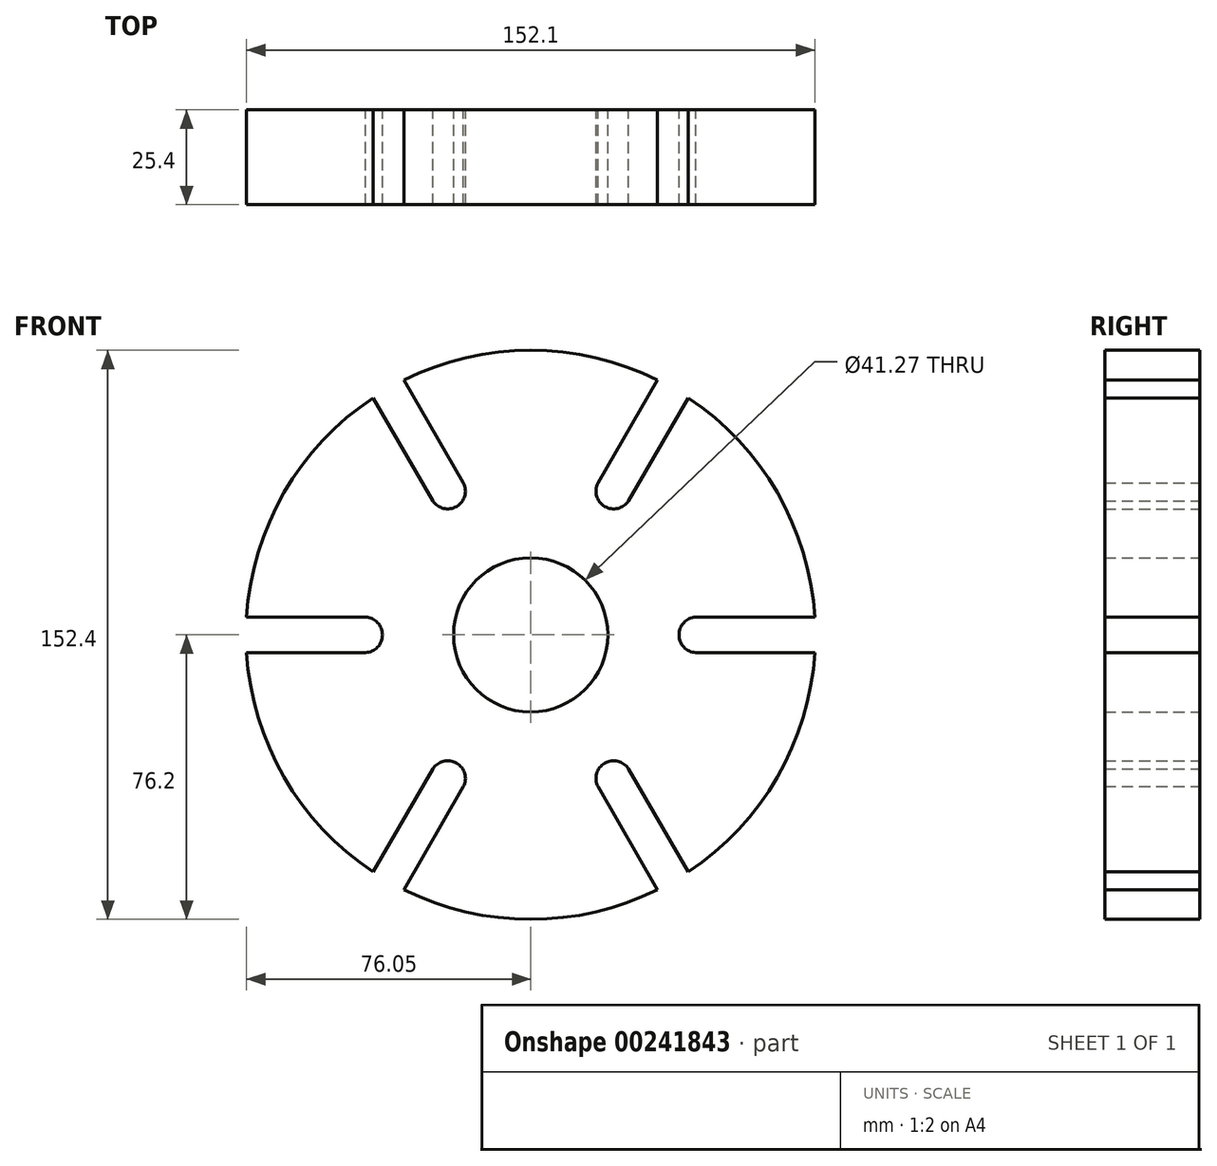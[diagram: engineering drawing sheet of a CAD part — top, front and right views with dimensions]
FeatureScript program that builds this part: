
annotation { "Feature Type Name" : "Feature", "Feature Type Description" : "" }
export const myFeature = defineFeature(function(context is Context, id is Id, definition is map)
    precondition{}
    {
        {
            var Q0;
            Q0=qCreatedBy(makeId("Front.planeOp"),FACE);
            var sketch = newSketch(context, id + "F0", { "sketchPlane" : qUnion([Q0])});
            skArc(sketch, "E0", {"start": v(-33.9, -68.24) * mm, "mid": v(0, -76.2) * mm, "end": v(33.9, -68.24) * mm});
            skArc(sketch, "E1", {"start": v(-17.98, -40.65) * mm, "mid": v(0, -44.45) * mm, "end": v(17.98, -40.65) * mm});
            skCircle(sketch, "E2", {"center": v(0, 0) * mm, "radius": 20.64 * mm});
            skLineSegment(sketch, "E3", {"start": v(0, 76.2) * mm, "end": v(0, -76.2) * mm});
            skLineSegment(sketch, "E4", {"start": v(-76.2, 0) * mm, "end": v(76.2, 0) * mm});
            skLineSegment(sketch, "E5", {"start": v(0, 0) * mm, "end": v(-38.1, -66) * mm});
            skLineSegment(sketch, "E6", {"start": v(0, 0) * mm, "end": v(-66, -38.1) * mm});
            skLineSegment(sketch, "E7", {"start": v(-38.1, 66) * mm, "end": v(0, 0) * mm});
            skLineSegment(sketch, "E8", {"start": v(-66, 38.1) * mm, "end": v(0, 0) * mm});
            skLineSegment(sketch, "E9.MirrorCS", {"start": v(0, 0) * mm, "end": v(38.1, -66) * mm});
            skLineSegment(sketch, "E10.MirrorCS", {"start": v(0, 0) * mm, "end": v(66, -38.1) * mm});
            skLineSegment(sketch, "E11.MirrorCS", {"start": v(38.1, 66) * mm, "end": v(0, 0) * mm});
            skLineSegment(sketch, "E12.MirrorCS", {"start": v(66, 38.1) * mm, "end": v(0, 0) * mm});
            skArc(sketch, "E13", {"start": v(-18.23, -41.1) * mm, "mid": v(-19.84, -34.37) * mm, "end": v(-26.47, -36.34) * mm});
            skLineSegment(sketch, "E14", {"start": v(-26.22, -35.9) * mm, "end": v(-42.14, -63.48) * mm});
            skLineSegment(sketch, "E15.MirrorCS", {"start": v(-17.98, -40.65) * mm, "end": v(-33.9, -68.24) * mm});
            skLineSegment(sketch, "E16.1.0", {"start": v(17.98, -40.65) * mm, "end": v(33.9, -68.24) * mm});
            skArc(sketch, "E16.1.1", {"start": v(26.47, -36.34) * mm, "mid": v(19.84, -34.37) * mm, "end": v(18.23, -41.1) * mm});
            skLineSegment(sketch, "E16.1.2", {"start": v(26.22, -35.9) * mm, "end": v(42.14, -63.48) * mm});
            skLineSegment(sketch, "E16.2.0", {"start": v(44.2, -4.76) * mm, "end": v(76.05, -4.76) * mm});
            skArc(sketch, "E16.2.1", {"start": v(44.7, 4.76) * mm, "mid": v(39.69, 0) * mm, "end": v(44.7, -4.76) * mm});
            skLineSegment(sketch, "E16.2.2", {"start": v(44.2, 4.76) * mm, "end": v(76.05, 4.76) * mm});
            skLineSegment(sketch, "E16.3.0", {"start": v(26.22, 35.9) * mm, "end": v(42.14, 63.48) * mm});
            skArc(sketch, "E16.3.1", {"start": v(18.23, 41.1) * mm, "mid": v(19.84, 34.37) * mm, "end": v(26.47, 36.34) * mm});
            skLineSegment(sketch, "E16.3.2", {"start": v(17.98, 40.65) * mm, "end": v(33.9, 68.24) * mm});
            skLineSegment(sketch, "E16.4.0", {"start": v(-17.98, 40.65) * mm, "end": v(-33.9, 68.24) * mm});
            skArc(sketch, "E16.4.1", {"start": v(-26.47, 36.34) * mm, "mid": v(-19.84, 34.37) * mm, "end": v(-18.23, 41.1) * mm});
            skLineSegment(sketch, "E16.4.2", {"start": v(-26.22, 35.9) * mm, "end": v(-42.14, 63.48) * mm});
            skLineSegment(sketch, "E16.5.0", {"start": v(-44.2, 4.76) * mm, "end": v(-76.05, 4.76) * mm});
            skArc(sketch, "E16.5.1", {"start": v(-44.7, -4.76) * mm, "mid": v(-39.69, 0) * mm, "end": v(-44.7, 4.76) * mm});
            skLineSegment(sketch, "E16.5.2", {"start": v(-44.2, -4.76) * mm, "end": v(-76.05, -4.76) * mm});
            skArc(sketch, "E17.trimOffspring", {"start": v(-76.05, -4.76) * mm, "mid": v(-66, -38.1) * mm, "end": v(-42.14, -63.48) * mm});
            skArc(sketch, "E18.trimOffspring", {"start": v(-44.2, -4.76) * mm, "mid": v(-38.5, -22.22) * mm, "end": v(-26.22, -35.9) * mm});
            skArc(sketch, "E19.trimOffspring", {"start": v(-42.14, 63.48) * mm, "mid": v(-66, 38.1) * mm, "end": v(-76.05, 4.76) * mm});
            skArc(sketch, "E20.trimOffspring", {"start": v(-26.22, 35.9) * mm, "mid": v(-38.5, 22.23) * mm, "end": v(-44.2, 4.76) * mm});
            skArc(sketch, "E21.trimOffspring", {"start": v(17.98, 40.65) * mm, "mid": v(0, 44.45) * mm, "end": v(-17.98, 40.65) * mm});
            skArc(sketch, "E22.trimOffspring", {"start": v(33.9, 68.24) * mm, "mid": v(0, 76.2) * mm, "end": v(-33.9, 68.24) * mm});
            skArc(sketch, "E23.trimOffspring", {"start": v(76.05, 4.76) * mm, "mid": v(66, 38.1) * mm, "end": v(42.14, 63.48) * mm});
            skArc(sketch, "E24.trimOffspring", {"start": v(44.2, 4.76) * mm, "mid": v(38.5, 22.23) * mm, "end": v(26.22, 35.9) * mm});
            skArc(sketch, "E25.trimOffspring", {"start": v(42.14, -63.48) * mm, "mid": v(66, -38.1) * mm, "end": v(76.05, -4.76) * mm});
            skArc(sketch, "E26.trimOffspring", {"start": v(26.22, -35.9) * mm, "mid": v(38.5, -22.23) * mm, "end": v(44.2, -4.76) * mm});
            skSolve(sketch);
        }
        {
            var Q0;
            Q0 = qSketchRegion(id + "F0", true);
            extrude(context, id + "F1", {"entities" : qUnion([Q0]), "depth" : 25.4 * mm});
        }
    });
